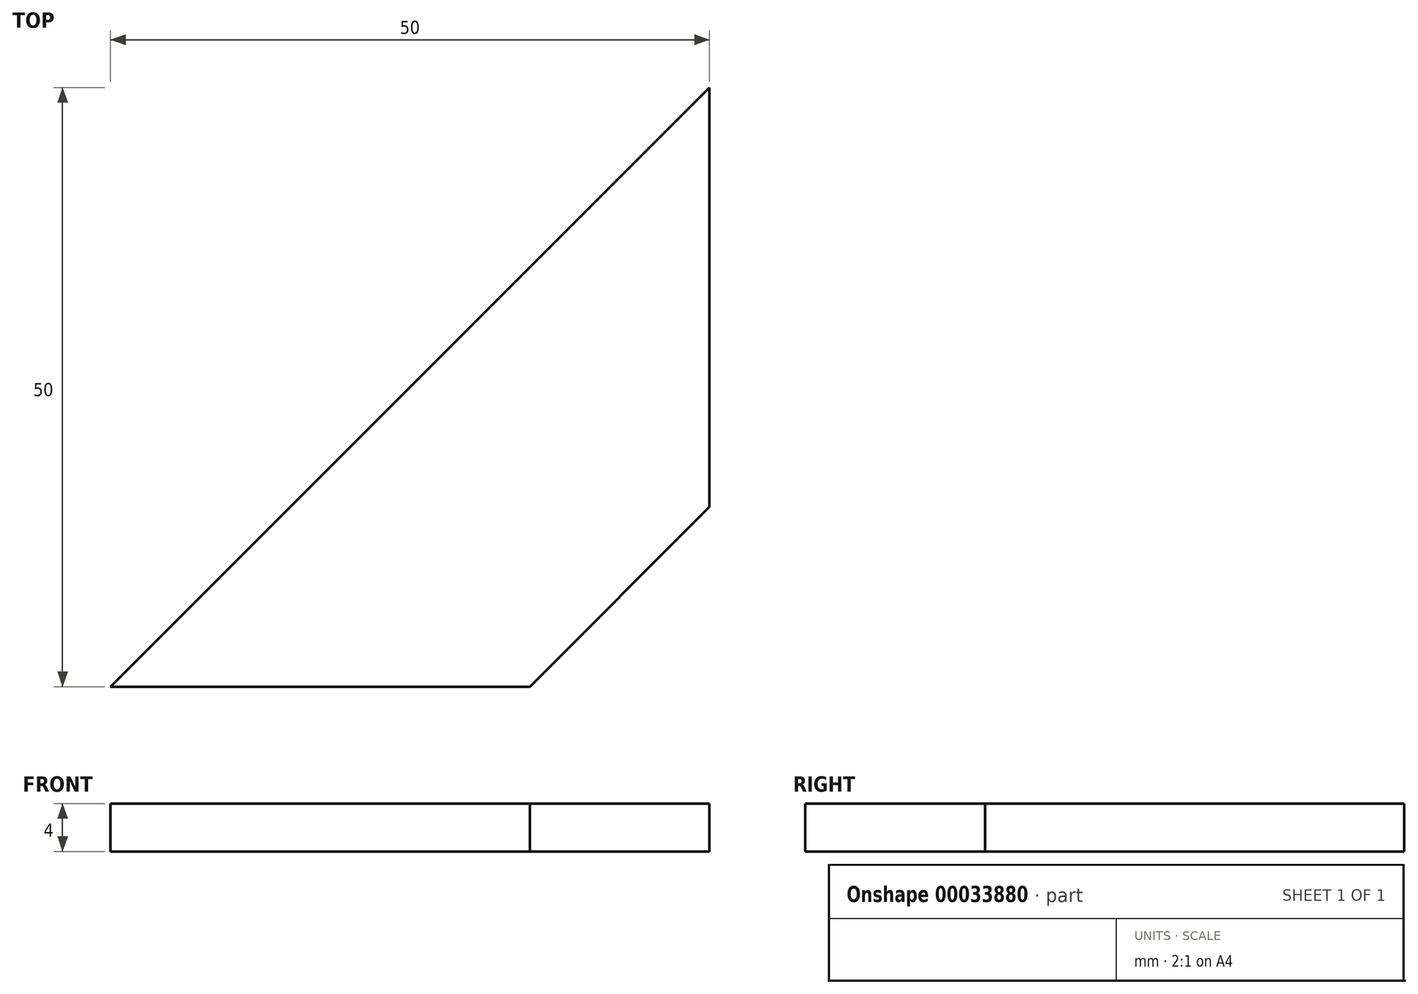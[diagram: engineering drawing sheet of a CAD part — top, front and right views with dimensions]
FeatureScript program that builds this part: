
annotation { "Feature Type Name" : "Feature", "Feature Type Description" : "" }
export const myFeature = defineFeature(function(context is Context, id is Id, definition is map)
    precondition{}
    {
        {
            var Q0;
            Q0=qCreatedBy(makeId("Top.planeOp"),FACE);
            var sketch = newSketch(context, id + "F0", { "sketchPlane" : qUnion([Q0])});
            skLineSegment(sketch, "E0", {"start": v(0, 0) * mm, "end": v(50, 50) * mm});
            skLineSegment(sketch, "E1", {"start": v(50, 50) * mm, "end": v(50, 0) * mm});
            skLineSegment(sketch, "E2", {"start": v(50, 0) * mm, "end": v(0, 0) * mm});
            skLineSegment(sketch, "E3", {"start": v(35, 0) * mm, "end": v(50, 15) * mm});
            skSolve(sketch);
        }
        {
            var Q0;
            Q0=makeQuery(id+"F0.imprint","IMPRINT",FACE,{"disambiguationData":[TD([[makeQuery(id+"F0.imprint","IMPRINT",EDGE,{"derivedFrom":sQuery(id+"F0.wireOp",EDGE,"E0")}),-1.0]])]});
            extrude(context, id + "F1", {"entities" : qUnion([Q0]), "depth" : 4 * mm, "symmetric" : true});
        }
    });
